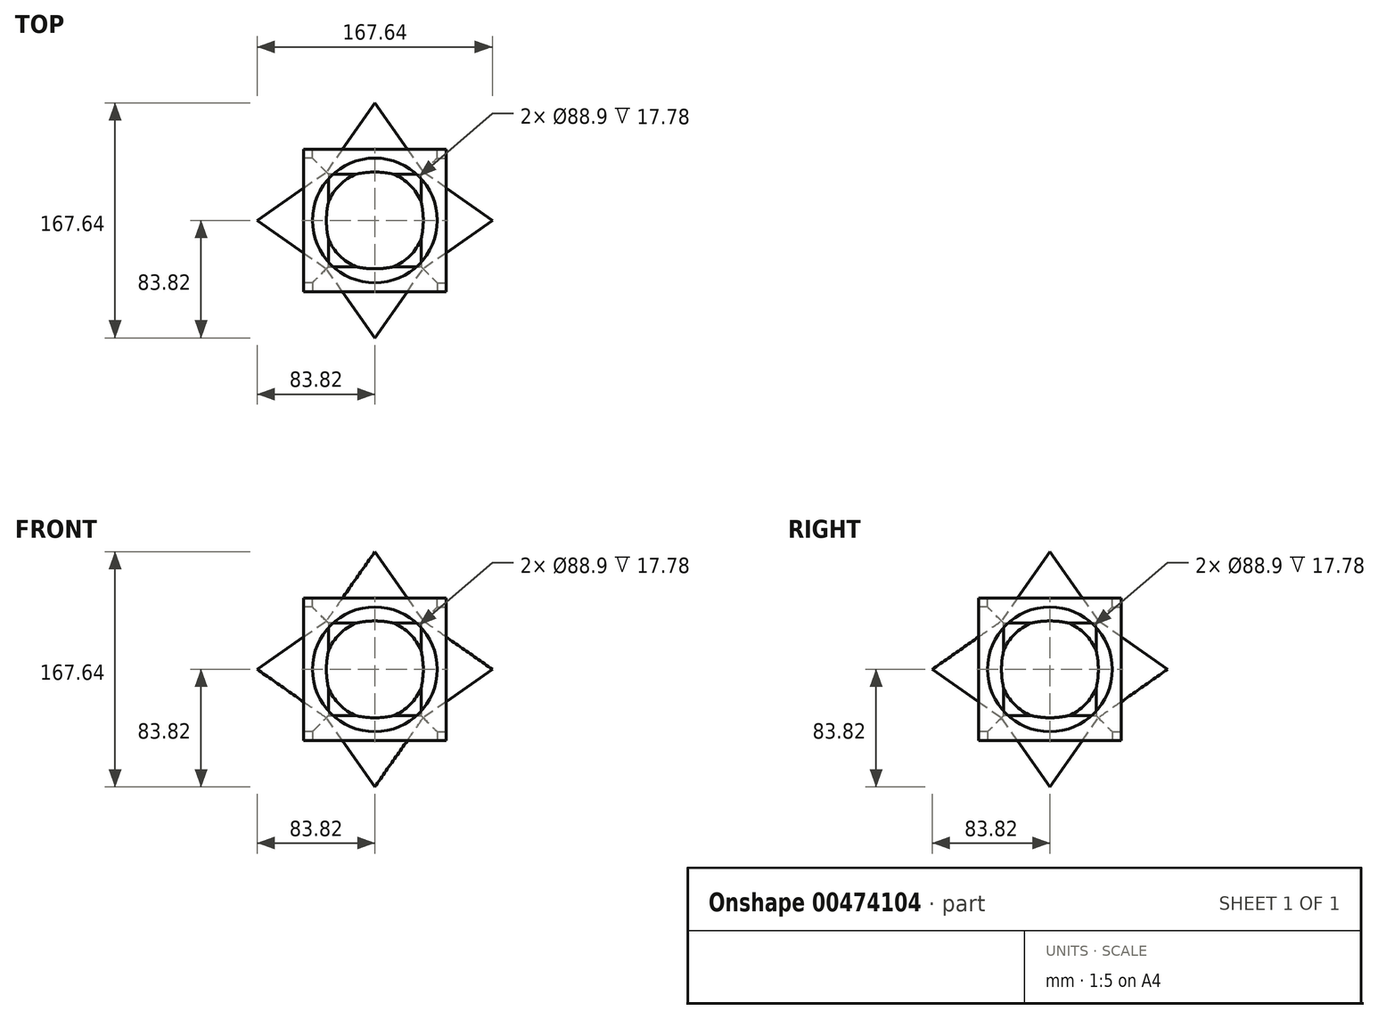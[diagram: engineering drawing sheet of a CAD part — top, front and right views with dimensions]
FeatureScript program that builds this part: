
annotation { "Feature Type Name" : "Feature", "Feature Type Description" : "" }
export const myFeature = defineFeature(function(context is Context, id is Id, definition is map)
    precondition{}
    {
        {
            var Q0;
            Q0=qCreatedBy(makeId("Front.planeOp"),FACE);
            var sketch = newSketch(context, id + "F0", { "sketchPlane" : qUnion([Q0])});
            skLineSegment(sketch, "E0.bottom", {"start": v(-50.8, 50.8) * mm, "end": v(50.8, 50.8) * mm});
            skLineSegment(sketch, "E0.top", {"start": v(-50.8, -50.8) * mm, "end": v(50.8, -50.8) * mm});
            skLineSegment(sketch, "E0.left", {"start": v(-50.8, 50.8) * mm, "end": v(-50.8, -50.8) * mm});
            skLineSegment(sketch, "E0.right", {"start": v(50.8, 50.8) * mm, "end": v(50.8, -50.8) * mm});
            skSolve(sketch);
        }
        {
            var Q0;
            Q0=makeQuery(id+"F0.imprint","IMPRINT",FACE,{"disambiguationData":[TD([[makeQuery(id+"F0.imprint","IMPRINT",EDGE,{"derivedFrom":sQuery(id+"F0.wireOp",EDGE,"E0.bottom")}),-1.0]])]});
            extrude(context, id + "F1", {"entities" : qUnion([Q0]), "endBound" : BoundingType.SYMMETRIC, "depth" : 101.6 * mm});
        }
        {
            var Q0;
            Q0=makeQuery(id+"F1.opExtrude","CAP_FACE",FACE,{"disambiguationData":[OSD([sQuery(id+"F0.wireOp",EDGE,"E0.bottom"),sQuery(id+"F0.wireOp",EDGE,"E0.top"),sQuery(id+"F0.wireOp",EDGE,"E0.left"),sQuery(id+"F0.wireOp",EDGE,"E0.right")])],"isStart":false});
            var sketch = newSketch(context, id + "F2", { "sketchPlane" : qUnion([Q0])});
            skCircle(sketch, "E1", {"center": v(0, 0) * mm, "radius": 44.45 * mm});
            skSolve(sketch);
        }
        {
            var Q0;
            Q0=makeQuery(id+"F2.imprint","IMPRINT",FACE,{"disambiguationData":[TD([[makeQuery(id+"F2.imprint","IMPRINT",EDGE,{"derivedFrom":sQuery(id+"F2.wireOp",EDGE,"E1")}),1.0]])]});
            extrude(context, id + "F3", {"entities" : qUnion([Q0]), "operationType" : NewBodyOperationType.REMOVE, "oppositeDirection" : true, "depth" : 17.78 * mm});
        }
        {
            var Q0;
            Q0=makeQuery(id+"F1.opExtrude","SWEPT_FACE",FACE,{"disambiguationData":[OSD([sQuery(id+"F0.wireOp",EDGE,"E0.top")])]});
            var sketch = newSketch(context, id + "F4", { "sketchPlane" : qUnion([Q0])});
            skCircle(sketch, "E2", {"center": v(0, 0) * mm, "radius": 44.45 * mm});
            skPoint(sketch, "E2.centerSnap0", {"position": v(50.8, 0) * mm});
            skPoint(sketch, "E2.centerSnap1", {"position": v(0, 50.8) * mm});
            skSolve(sketch);
        }
        {
            var Q0;
            Q0=makeQuery(id+"F4.imprint","IMPRINT",FACE,{"disambiguationData":[TD([[makeQuery(id+"F4.imprint","IMPRINT",EDGE,{"derivedFrom":sQuery(id+"F4.wireOp",EDGE,"E2")}),1.0]])]});
            extrude(context, id + "F5", {"entities" : qUnion([Q0]), "operationType" : NewBodyOperationType.REMOVE, "oppositeDirection" : true, "depth" : 17.78 * mm});
        }
        {
            var Q0;
            Q0=makeQuery(id+"F1.opExtrude","SWEPT_FACE",FACE,{"disambiguationData":[OSD([sQuery(id+"F0.wireOp",EDGE,"E0.right")])]});
            var sketch = newSketch(context, id + "F6", { "sketchPlane" : qUnion([Q0])});
            skCircle(sketch, "E3", {"center": v(0, 0) * mm, "radius": 44.45 * mm});
            skPoint(sketch, "E3.centerSnap0", {"position": v(0, 50.8) * mm});
            skSolve(sketch);
        }
        {
            var Q0;
            Q0=makeQuery(id+"F6.imprint","IMPRINT",FACE,{"disambiguationData":[TD([[makeQuery(id+"F6.imprint","IMPRINT",EDGE,{"derivedFrom":sQuery(id+"F6.wireOp",EDGE,"E3")}),1.0]])]});
            extrude(context, id + "F7", {"entities" : qUnion([Q0]), "operationType" : NewBodyOperationType.REMOVE, "oppositeDirection" : true, "depth" : 17.78 * mm});
        }
        {
            var Q0;
            Q0=makeQuery(id+"F1.opExtrude","SWEPT_FACE",FACE,{"disambiguationData":[OSD([sQuery(id+"F0.wireOp",EDGE,"E0.bottom")])]});
            var sketch = newSketch(context, id + "F8", { "sketchPlane" : qUnion([Q0])});
            skCircle(sketch, "E4", {"center": v(0, 0) * mm, "radius": 44.45 * mm});
            skPoint(sketch, "E4.centerSnap0", {"position": v(-50.8, 0) * mm});
            skSolve(sketch);
        }
        {
            var Q0;
            Q0=makeQuery(id+"F8.imprint","IMPRINT",FACE,{"disambiguationData":[TD([[makeQuery(id+"F8.imprint","IMPRINT",EDGE,{"derivedFrom":sQuery(id+"F8.wireOp",EDGE,"E4")}),1.0]])]});
            extrude(context, id + "F9", {"entities" : qUnion([Q0]), "operationType" : NewBodyOperationType.REMOVE, "oppositeDirection" : true, "depth" : 17.78 * mm});
        }
        {
            var Q0;
            Q0=makeQuery(id+"F1.opExtrude","CAP_FACE",FACE,{"disambiguationData":[OSD([sQuery(id+"F0.wireOp",EDGE,"E0.bottom"),sQuery(id+"F0.wireOp",EDGE,"E0.top"),sQuery(id+"F0.wireOp",EDGE,"E0.left"),sQuery(id+"F0.wireOp",EDGE,"E0.right")])],"isStart":true});
            var sketch = newSketch(context, id + "F10", { "sketchPlane" : qUnion([Q0])});
            skCircle(sketch, "E5", {"center": v(0, 0) * mm, "radius": 44.45 * mm});
            skSolve(sketch);
        }
        {
            var Q0;
            Q0=makeQuery(id+"F10.imprint","IMPRINT",FACE,{"disambiguationData":[TD([[makeQuery(id+"F10.imprint","IMPRINT",EDGE,{"derivedFrom":sQuery(id+"F10.wireOp",EDGE,"E5")}),1.0]])]});
            extrude(context, id + "F11", {"entities" : qUnion([Q0]), "operationType" : NewBodyOperationType.REMOVE, "oppositeDirection" : true, "depth" : 17.78 * mm});
        }
        {
            var Q0;
            Q0=makeQuery(id+"F1.opExtrude","SWEPT_FACE",FACE,{"disambiguationData":[OSD([sQuery(id+"F0.wireOp",EDGE,"E0.left")])]});
            var sketch = newSketch(context, id + "F12", { "sketchPlane" : qUnion([Q0])});
            skCircle(sketch, "E6", {"center": v(0, 0) * mm, "radius": 44.45 * mm});
            skPoint(sketch, "E6.centerSnap0", {"position": v(0, 50.8) * mm});
            skSolve(sketch);
        }
        {
            var Q0;
            Q0=makeQuery(id+"F12.imprint","IMPRINT",FACE,{"disambiguationData":[TD([[makeQuery(id+"F12.imprint","IMPRINT",EDGE,{"derivedFrom":sQuery(id+"F12.wireOp",EDGE,"E6")}),1.0]])]});
            extrude(context, id + "F13", {"entities" : qUnion([Q0]), "operationType" : NewBodyOperationType.REMOVE, "oppositeDirection" : true, "depth" : 17.78 * mm});
        }
        {
            var Q0;
            Q0=qCreatedBy(makeId("Front.planeOp"),FACE);
            var sketch = newSketch(context, id + "F14", { "sketchPlane" : qUnion([Q0])});
            skLineSegment(sketch, "E7", {"start": v(0, 33.02) * mm, "end": v(-35.56, 33.02) * mm});
            skLineSegment(sketch, "E8", {"start": v(-35.56, 33.02) * mm, "end": v(0, 83.82) * mm});
            skLineSegment(sketch, "E9", {"start": v(0, 83.82) * mm, "end": v(0, 33.02) * mm});
            skLineSegment(sketch, "E10", {"start": v(0, -33.02) * mm, "end": v(35.56, -33.02) * mm});
            skLineSegment(sketch, "E11", {"start": v(35.56, -33.02) * mm, "end": v(0, -83.82) * mm});
            skLineSegment(sketch, "E12", {"start": v(0, -83.82) * mm, "end": v(0, -33.02) * mm});
            skSolve(sketch);
        }
        {
            var Q0;
            Q0=makeQuery(id+"F14.imprint","IMPRINT",FACE,{"disambiguationData":[TD([[makeQuery(id+"F14.imprint","IMPRINT",EDGE,{"derivedFrom":sQuery(id+"F14.wireOp",EDGE,"E7")}),-1.0]])]});
            var Q1;
            Q1=makeQuery(id+"F14.imprint","IMPRINT",FACE,{"disambiguationData":[TD([[makeQuery(id+"F14.imprint","IMPRINT",EDGE,{"derivedFrom":sQuery(id+"F14.wireOp",EDGE,"E10")}),-1.0]])]});
            var Q2;
            Q2=sQuery(id+"F14.wireOp",EDGE,"E12");
            revolve(context, id + "F15", {"operationType" : NewBodyOperationType.ADD, "entities" : qUnion([Q0, Q1]), "axis" : qUnion([Q2]), "revolveType" : RevolveType.FULL});
        }
        {
            var Q0;
            Q0=qCreatedBy(makeId("Front.planeOp"),FACE);
            var sketch = newSketch(context, id + "F16", { "sketchPlane" : qUnion([Q0])});
            skLineSegment(sketch, "E13", {"start": v(-33.02, 0) * mm, "end": v(-33.02, 35.56) * mm});
            skLineSegment(sketch, "E14", {"start": v(-33.02, 35.56) * mm, "end": v(-83.82, 0) * mm});
            skLineSegment(sketch, "E15", {"start": v(-83.82, 0) * mm, "end": v(-33.02, 0) * mm});
            skLineSegment(sketch, "E16", {"start": v(33.02, 0) * mm, "end": v(33.02, -35.56) * mm});
            skLineSegment(sketch, "E17", {"start": v(33.02, -35.56) * mm, "end": v(83.82, 0) * mm});
            skLineSegment(sketch, "E18", {"start": v(83.82, 0) * mm, "end": v(33.02, 0) * mm});
            skSolve(sketch);
        }
        {
            var Q0;
            Q0=makeQuery(id+"F16.imprint","IMPRINT",FACE,{"disambiguationData":[TD([[makeQuery(id+"F16.imprint","IMPRINT",EDGE,{"derivedFrom":sQuery(id+"F16.wireOp",EDGE,"E13")}),1.0]])]});
            var Q1;
            Q1=makeQuery(id+"F16.imprint","IMPRINT",FACE,{"disambiguationData":[TD([[makeQuery(id+"F16.imprint","IMPRINT",EDGE,{"derivedFrom":sQuery(id+"F16.wireOp",EDGE,"E16")}),1.0]])]});
            var Q2;
            Q2=sQuery(id+"F16.wireOp",EDGE,"E18");
            revolve(context, id + "F17", {"operationType" : NewBodyOperationType.ADD, "entities" : qUnion([Q0, Q1]), "axis" : qUnion([Q2]), "revolveType" : RevolveType.FULL});
        }
        {
            var Q0;
            Q0=qCreatedBy(makeId("Right.planeOp"),FACE);
            var sketch = newSketch(context, id + "F18", { "sketchPlane" : qUnion([Q0])});
            skLineSegment(sketch, "E19", {"start": v(-33.02, 0) * mm, "end": v(-33.02, 35.56) * mm});
            skLineSegment(sketch, "E20", {"start": v(-33.02, 35.56) * mm, "end": v(-83.82, 0) * mm});
            skLineSegment(sketch, "E21", {"start": v(-83.82, 0) * mm, "end": v(-33.02, 0) * mm});
            skLineSegment(sketch, "E22", {"start": v(33.02, 0) * mm, "end": v(33.02, -35.56) * mm});
            skLineSegment(sketch, "E23", {"start": v(33.02, -35.56) * mm, "end": v(83.82, 0) * mm});
            skLineSegment(sketch, "E24", {"start": v(83.82, 0) * mm, "end": v(33.02, 0) * mm});
            skSolve(sketch);
        }
        {
            var Q0;
            Q0=makeQuery(id+"F18.imprint","IMPRINT",FACE,{"disambiguationData":[TD([[makeQuery(id+"F18.imprint","IMPRINT",EDGE,{"derivedFrom":sQuery(id+"F18.wireOp",EDGE,"E19")}),1.0]])]});
            var Q1;
            Q1=makeQuery(id+"F18.imprint","IMPRINT",FACE,{"disambiguationData":[TD([[makeQuery(id+"F18.imprint","IMPRINT",EDGE,{"derivedFrom":sQuery(id+"F18.wireOp",EDGE,"E22")}),1.0]])]});
            var Q2;
            Q2=sQuery(id+"F18.wireOp",EDGE,"E24");
            revolve(context, id + "F19", {"operationType" : NewBodyOperationType.ADD, "entities" : qUnion([Q0, Q1]), "axis" : qUnion([Q2]), "revolveType" : RevolveType.FULL});
        }
    });
